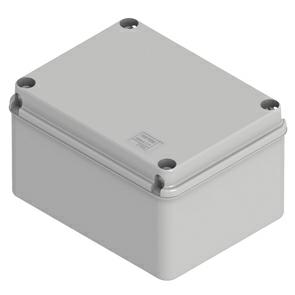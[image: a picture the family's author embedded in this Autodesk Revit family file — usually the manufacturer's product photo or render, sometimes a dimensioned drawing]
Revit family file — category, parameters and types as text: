
# Revit family: Building-ContenitoriParete-GEWISS-44CE-CASSETTE-DERIVAZIONE-PARETE_ALTA_CAPIENZA
name_source: partatom
category: Apparecchi elettrici
revit_build: Autodesk Revit 2016 (Build: 20161004_0715(x64)
units: mm (PartAtom-declared; Revit-internal decimal feet)

## family parameters
Condiviso = No
Host = Superficie
Mantenere orientamento annotazione = Sì
Numero OmniClass = 23.80.30.14.24
Punto di calcolo locali = Sì
Quota connettore circolare = Usa diametro
Taglio con vuoti quando caricato = No
Tipo di parte = Normale
Titolo OmniClass = Junction Boxes

## types (1)
- Building-ContenitoriParete-GEWISS-44CE-CASSETTE-DERIVAZIONE-PARETE_ALTA_CAPIENZA
    Accessori per ripristino isolamento = GW44621, GW44623
    Altezza utile fondo = 119 mm
    Applicazione = Derivazioni ordinarie
    Carico apparente = 0 VA
    Catalogo = BUILDING
    Catalogo Serie = 44 CE
    Classe isolamento = II (secondo Norma IEC 61140)
    Classificazione = Other
    Codice EAN = 8011564763562
    Codice Electrocod = 02210
    Colore = Grigio RAL 7035
    Colore coperchio = Trasparente
    Coperchio = Basso a vite
    Coperchio_ = GEWISS COPERCHIO TRASPARENTE
    Coppia serraggio viti = 1,8NM
    Descrizione = CASS.IP56 FONDO ALTO COP.TRA.380X300X170
    Dettaglio = Elemento di dettaglio - 44CE alta capienza : 380x300x120
    Dim. interne BxHxP (mm) = 380x300x170
    GEWISS SCHEDA TECNICA = http://pro.gewiss.com
    Glow Wire Test = 650°C
    Grado di protezione = IP56
    IDF = 302224ff-32ff-4c10-8234-0240c66b2a60
    IDT = 54e6e708-f22e-4f1e-b852-9ec59277bb73
    Immagine tipo = GW44140.jpg
    Larghezza_interna = 380 mm
    Lunghezza_interna = 300 mm
    Materiale = Tecnopolimero GWPLAST 75
    Modello = GW44140
    Pareti = Lisce
    Produttore = GEWISS S.p.A.
    Prospetto di default = 1219 mm
    Resistenza agli urti = IK08
    SEO = Cassetta
    Scatola_ = GEWISS SCATOLA
    Scheda Tecnica = https://www.gewiss.com
    Spessore = 170 mm  [stored 0.557743 ft]
    Temperatura di impiego = -25 +60 °C
    Termopressione con biglia = 85 °C
    Tipo Materiale = Halogen free secondo norma EN 60754-2
    Tipo fondo = Alta capienza
    URL = https://www.gewiss.com
    Versione file RFA = 18.0
    Viti coperchio (n. e Tipo) = 4 isol. a cerniera piombabili
    Voltaggio_x = 0 V
    Ã˜ max fori eseguibili = 54MM

note: [stored X ft] marks values corroborated as IEEE doubles in the binary element streams (Revit-internal decimal feet)

## geometry (parser evidence)
native form markers: Blend x4
no freeform markers — native parametric forms only
